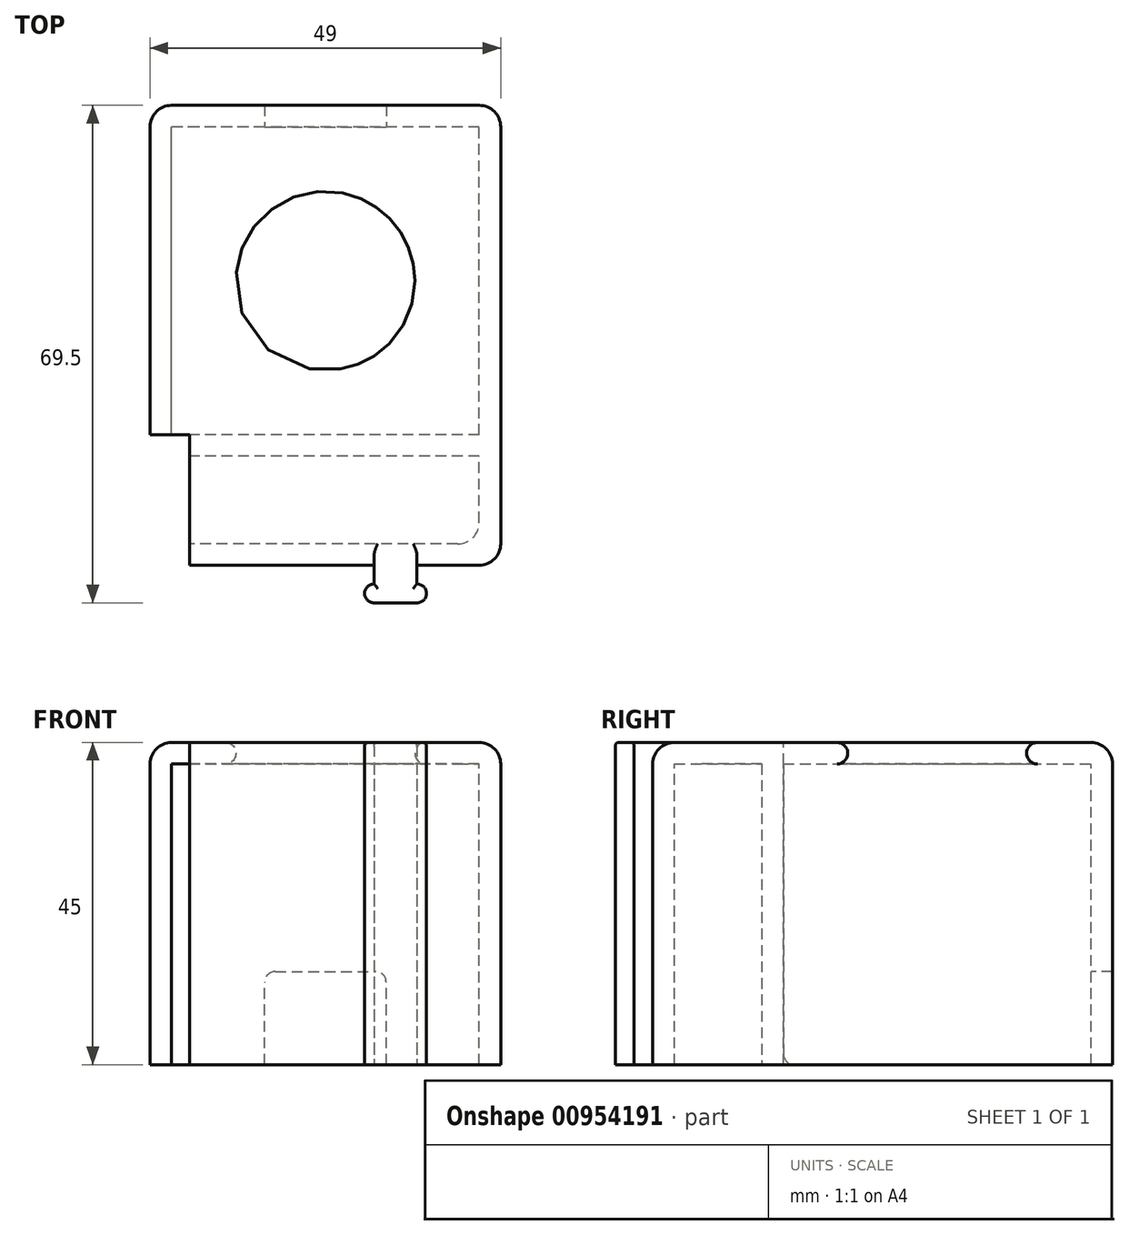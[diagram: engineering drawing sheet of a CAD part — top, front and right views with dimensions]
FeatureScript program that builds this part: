
annotation { "Feature Type Name" : "Feature", "Feature Type Description" : "" }
export const myFeature = defineFeature(function(context is Context, id is Id, definition is map)
    precondition{}
    {
        {
            var Q0;
            Q0=qCreatedBy(makeId("Top.planeOp"),FACE);
            var sketch = newSketch(context, id + "F0", { "sketchPlane" : qUnion([Q0])});
            skLineSegment(sketch, "E0.bottom", {"start": v(21.5, -21.5) * mm, "end": v(-21.5, -21.5) * mm});
            skLineSegment(sketch, "E0.top", {"start": v(21.5, 21.5) * mm, "end": v(-21.5, 21.5) * mm});
            skLineSegment(sketch, "E0.left", {"start": v(21.5, -21.5) * mm, "end": v(21.5, 21.5) * mm});
            skLineSegment(sketch, "E0.right", {"start": v(-21.5, -21.5) * mm, "end": v(-21.5, 21.5) * mm});
            skPoint(sketch, "E0.middle", {"position": v(0, 0) * mm});
            skLineSegment(sketch, "E1.0", {"start": v(24.5, -24.5) * mm, "end": v(24.5, 24.5) * mm});
            skLineSegment(sketch, "E1.1", {"start": v(24.5, -24.5) * mm, "end": v(-24.5, -24.5) * mm});
            skLineSegment(sketch, "E1.2", {"start": v(-24.5, -24.5) * mm, "end": v(-24.5, 24.5) * mm});
            skLineSegment(sketch, "E1.3", {"start": v(24.5, 24.5) * mm, "end": v(-24.5, 24.5) * mm});
            skSolve(sketch);
        }
        {
            var Q0;
            Q0=makeQuery(id+"F0.imprint","IMPRINT",FACE,{"disambiguationData":[TD([[makeQuery(id+"F0.imprint","IMPRINT",EDGE,{"derivedFrom":sQuery(id+"F0.wireOp",EDGE,"E0.bottom")}),1.0]])]});
            extrude(context, id + "F1", {"entities" : qUnion([Q0]), "oppositeDirection" : true, "depth" : 42 * mm, "offsetDistance" : 25 * mm});
        }
        {
            var Q0;
            Q0=makeQuery(id+"F0.imprint","IMPRINT",FACE,{"disambiguationData":[TD([[makeQuery(id+"F0.imprint","IMPRINT",EDGE,{"derivedFrom":sQuery(id+"F0.wireOp",EDGE,"E0.bottom")}),-1.0]])]});
            var Q1;
            Q1=makeQuery(id+"F0.imprint","IMPRINT",FACE,{"disambiguationData":[TD([[makeQuery(id+"F0.imprint","IMPRINT",EDGE,{"derivedFrom":sQuery(id+"F0.wireOp",EDGE,"E0.bottom")}),1.0]])]});
            extrude(context, id + "F2", {"entities" : qUnion([Q0, Q1]), "operationType" : NewBodyOperationType.ADD, "depth" : 3 * mm, "offsetDistance" : 25 * mm});
        }
        {
            var Q0;
            Q0=qCreatedBy(makeId("Top.planeOp"),FACE);
            var sketch = newSketch(context, id + "F3", { "sketchPlane" : qUnion([Q0])});
            skCircle(sketch, "E2", {"center": v(0, 0) * mm, "radius": 12.5 * mm});
            skSolve(sketch);
        }
        {
            var Q0;
            Q0=qSketchRegion(id+"F3",true);
            extrude(context, id + "F4", {"entities" : qUnion([Q0]), "operationType" : NewBodyOperationType.REMOVE, "endBound" : BoundingType.THROUGH_ALL, "depth" : 25 * mm, "offsetDistance" : 25 * mm});
        }
        {
            var Q0;
            Q0=qCreatedBy(makeId("Front.planeOp"),FACE);
            var sketch = newSketch(context, id + "F5", { "sketchPlane" : qUnion([Q0])});
            skLineSegment(sketch, "E3.bottom", {"start": v(8.5, -29) * mm, "end": v(-8.5, -29) * mm});
            skLineSegment(sketch, "E4", {"start": v(8.5, -42) * mm, "end": v(-8.5, -42) * mm});
            skLineSegment(sketch, "E5", {"start": v(0, 0) * mm, "end": v(0, -42) * mm, "construction": true});
            skLineSegment(sketch, "E6", {"start": v(8.5, -29) * mm, "end": v(8.5, -42) * mm});
            skLineSegment(sketch, "E7", {"start": v(-8.5, -29) * mm, "end": v(-8.5, -42) * mm});
            skSolve(sketch);
        }
        {
            var Q0;
            Q0=qSketchRegion(id+"F5",true);
            extrude(context, id + "F6", {"entities" : qUnion([Q0]), "operationType" : NewBodyOperationType.REMOVE, "endBound" : BoundingType.THROUGH_ALL, "oppositeDirection" : true, "depth" : 25 * mm, "offsetDistance" : 25 * mm});
        }
        {
            var Q0;
            Q0=qCreatedBy(makeId("Top.planeOp"),FACE);
            var sketch = newSketch(context, id + "F7", { "sketchPlane" : qUnion([Q0])});
            skLineSegment(sketch, "E8.bottom", {"start": v(-24.5, -24.5) * mm, "end": v(24.5, -24.5) * mm});
            skLineSegment(sketch, "E8.top", {"start": v(-24.5, -39.75) * mm, "end": v(24.5, -39.75) * mm});
            skLineSegment(sketch, "E8.left", {"start": v(-24.5, -24.5) * mm, "end": v(-24.5, -39.75) * mm});
            skLineSegment(sketch, "E8.right", {"start": v(24.5, -24.5) * mm, "end": v(24.5, -39.75) * mm});
            skLineSegment(sketch, "E9.0", {"start": v(-21.5, -24.5) * mm, "end": v(-21.5, -36.75) * mm});
            skLineSegment(sketch, "E9.2", {"start": v(21.5, -24.5) * mm, "end": v(21.5, -36.75) * mm});
            skLineSegment(sketch, "E9.3", {"start": v(-21.5, -36.75) * mm, "end": v(21.5, -36.75) * mm});
            skSolve(sketch);
        }
        {
            var Q0;
            Q0=makeQuery(id+"F7.imprint","IMPRINT",FACE,{"disambiguationData":[TD([[makeQuery(id+"F7.imprint","IMPRINT",EDGE,{"derivedFrom":sQuery(id+"F7.wireOp",EDGE,"E8.bottom")}),-1.0]])]});
            var Q1;
            Q1=makeQuery(id+"F1.opExtrude","CAP_FACE",FACE,{"disambiguationData":[OSD([sQuery(id+"F0.wireOp",EDGE,"E0.bottom"),sQuery(id+"F0.wireOp",EDGE,"E0.top"),sQuery(id+"F0.wireOp",EDGE,"E0.left"),sQuery(id+"F0.wireOp",EDGE,"E0.right"),sQuery(id+"F0.wireOp",EDGE,"E1.0"),sQuery(id+"F0.wireOp",EDGE,"E1.1"),sQuery(id+"F0.wireOp",EDGE,"E1.2"),sQuery(id+"F0.wireOp",EDGE,"E1.3")])],"isStart":false});
            var Q2;
            Q2=makeQuery(id+"F2.opExtrude","CAP_FACE",FACE,{"disambiguationData":[OSD([sQuery(id+"F0.wireOp",EDGE,"E1.0"),sQuery(id+"F0.wireOp",EDGE,"E1.1"),sQuery(id+"F0.wireOp",EDGE,"E1.2"),sQuery(id+"F0.wireOp",EDGE,"E1.3")])],"isStart":false});
            extrude(context, id + "F8", {"entities" : qUnion([Q0]), "operationType" : NewBodyOperationType.ADD, "endBound" : BoundingType.UP_TO_SURFACE, "oppositeDirection" : true, "depth" : 25 * mm, "endBoundEntityFace" : qUnion([Q1]), "offsetDistance" : 25 * mm});
        }
        {
            var Q0;
            Q0=makeQuery(id+"F7.imprint","IMPRINT",FACE,{"disambiguationData":[TD([[makeQuery(id+"F7.imprint","IMPRINT",EDGE,{"derivedFrom":sQuery(id+"F7.wireOp",EDGE,"E9.0")}),1.0]])]});
            var Q1;
            Q1=makeQuery(id+"F7.imprint","IMPRINT",FACE,{"disambiguationData":[TD([[makeQuery(id+"F7.imprint","IMPRINT",EDGE,{"derivedFrom":sQuery(id+"F7.wireOp",EDGE,"E8.bottom")}),-1.0]])]});
            var Q2;
            Q2=makeQuery(id+"F2.opExtrude","CAP_FACE",FACE,{"disambiguationData":[OSD([sQuery(id+"F0.wireOp",EDGE,"E1.0"),sQuery(id+"F0.wireOp",EDGE,"E1.1"),sQuery(id+"F0.wireOp",EDGE,"E1.2"),sQuery(id+"F0.wireOp",EDGE,"E1.3")])],"isStart":false});
            extrude(context, id + "F9", {"entities" : qUnion([Q0, Q1]), "operationType" : NewBodyOperationType.ADD, "endBound" : BoundingType.UP_TO_SURFACE, "depth" : 25 * mm, "endBoundEntityFace" : qUnion([Q2]), "offsetDistance" : 25 * mm});
        }
        {
            var Q0;
            Q0=qCreatedBy(makeId("Top.planeOp"),FACE);
            var sketch = newSketch(context, id + "F10", { "sketchPlane" : qUnion([Q0])});
            skLineSegment(sketch, "E10.bottom", {"start": v(6.8, -39.75) * mm, "end": v(12.8, -39.75) * mm});
            skLineSegment(sketch, "E10.top", {"start": v(6.8, -45) * mm, "end": v(12.8, -45) * mm});
            skLineSegment(sketch, "E10.left", {"start": v(6.8, -39.75) * mm, "end": v(6.8, -42.35) * mm});
            skLineSegment(sketch, "E10.right", {"start": v(12.8, -39.75) * mm, "end": v(12.8, -42.35) * mm});
            skArc(sketch, "E11", {"start": v(6.8, -42.35) * mm, "mid": v(5.47, -43.68) * mm, "end": v(6.8, -45) * mm});
            skArc(sketch, "E12", {"start": v(12.8, -45) * mm, "mid": v(14.12, -43.68) * mm, "end": v(12.8, -42.35) * mm});
            skSolve(sketch);
        }
        {
            var Q0;
            Q0=qSketchRegion(id+"F10",true);
            var Q1;
            Q1=makeQuery(id+"F2.opExtrude","CAP_FACE",FACE,{"disambiguationData":[OSD([sQuery(id+"F0.wireOp",EDGE,"E1.0"),sQuery(id+"F0.wireOp",EDGE,"E1.1"),sQuery(id+"F0.wireOp",EDGE,"E1.2"),sQuery(id+"F0.wireOp",EDGE,"E1.3")])],"isStart":false});
            var Q2;
            Q2=makeQuery(id+"F1.opExtrude","CAP_FACE",FACE,{"disambiguationData":[OSD([sQuery(id+"F0.wireOp",EDGE,"E0.bottom"),sQuery(id+"F0.wireOp",EDGE,"E0.top"),sQuery(id+"F0.wireOp",EDGE,"E0.left"),sQuery(id+"F0.wireOp",EDGE,"E0.right"),sQuery(id+"F0.wireOp",EDGE,"E1.0"),sQuery(id+"F0.wireOp",EDGE,"E1.1"),sQuery(id+"F0.wireOp",EDGE,"E1.2"),sQuery(id+"F0.wireOp",EDGE,"E1.3")])],"isStart":false});
            extrude(context, id + "F11", {"entities" : qUnion([Q0]), "operationType" : NewBodyOperationType.ADD, "endBound" : BoundingType.UP_TO_SURFACE, "depth" : 25 * mm, "endBoundEntityFace" : qUnion([Q1]), "offsetDistance" : 25 * mm, "hasSecondDirection" : true, "secondDirectionBound" : SecondDirectionBoundingType.UP_TO_SURFACE, "secondDirectionOppositeDirection" : true, "secondDirectionDepth" : 25 * mm, "secondDirectionBoundEntityFace" : qUnion([Q2])});
        }
        {
            var Q0;
            Q0=qCreatedBy(makeId("Right.planeOp"),FACE);
            cPlane(context, id + "F12", {"entities" : qUnion([Q0]), "cplaneType" : CPlaneType.OFFSET, "offset" : 19 * mm, "oppositeDirection" : true, "width" : 150 * mm, "height" : 150 * mm});
        }
        {
            var Q0;
            Q0=qCreatedBy(id+"F12.planeOp",FACE);
            var sketch = newSketch(context, id + "F13", { "sketchPlane" : qUnion([Q0])});
            skLineSegment(sketch, "E13.bottom", {"start": v(-21.5, -42) * mm, "end": v(-39.75, -42) * mm});
            skLineSegment(sketch, "E13.top", {"start": v(-21.5, 3) * mm, "end": v(-39.75, 3) * mm});
            skLineSegment(sketch, "E13.left", {"start": v(-21.5, -42) * mm, "end": v(-21.5, 3) * mm});
            skLineSegment(sketch, "E13.right", {"start": v(-39.75, -42) * mm, "end": v(-39.75, 3) * mm});
            skSolve(sketch);
        }
        {
            var Q0;
            Q0=qSketchRegion(id+"F13",true);
            var Q1;
            {var subQ0=sQuery(id+"F7.wireOp",EDGE,"E8.left");var subQ1=sQuery(id+"F0.wireOp",EDGE,"E1.2");Q1=makeQuery(id+"F9.boolean.opBoolean","MERGE",FACE,{"derivedFrom":[makeQuery(id+"F8.boolean.opBoolean","MERGE",FACE,{"derivedFrom":[makeQuery(id+"F2.boolean.opBoolean","MERGE",FACE,{"derivedFrom":[makeQuery(id+"F1.opExtrude","SWEPT_FACE",FACE,{"disambiguationData":[OSD([subQ1])]}),makeQuery(id+"F2.opExtrude","SWEPT_FACE",FACE,{"disambiguationData":[OSD([subQ1])]})]}),makeQuery(id+"F8.opExtrude","SWEPT_FACE",FACE,{"disambiguationData":[OSD([subQ0])]})]}),makeQuery(id+"F9.opExtrude","SWEPT_FACE",FACE,{"disambiguationData":[OSD([subQ0])]})]});}
            extrude(context, id + "F14", {"entities" : qUnion([Q0]), "operationType" : NewBodyOperationType.REMOVE, "endBound" : BoundingType.UP_TO_SURFACE, "oppositeDirection" : true, "depth" : 25 * mm, "endBoundEntityFace" : qUnion([Q1]), "offsetDistance" : 10 * mm, "offsetOppositeDirection" : true});
        }
        {
            var Q0;
            Q0=makeQuery(id+"F1.opExtrude","SWEPT_EDGE",EDGE,{"disambiguationData":[OSD([sQuery(id+"F0.wireOp",EDGE,"E1.1"),sQuery(id+"F0.wireOp",EDGE,"E1.2")])]});
            var Q1;
            Q1=makeQuery(id+"F1.opExtrude","SWEPT_EDGE",EDGE,{"disambiguationData":[OSD([sQuery(id+"F0.wireOp",EDGE,"E1.0"),sQuery(id+"F0.wireOp",EDGE,"E1.1")])]});
            var Q2;
            Q2=makeQuery(id+"F1.opExtrude","SWEPT_EDGE",EDGE,{"disambiguationData":[OSD([sQuery(id+"F0.wireOp",EDGE,"E1.0"),sQuery(id+"F0.wireOp",EDGE,"E1.3")])]});
            var Q3;
            Q3=makeQuery(id+"F1.opExtrude","SWEPT_EDGE",EDGE,{"disambiguationData":[OSD([sQuery(id+"F0.wireOp",EDGE,"E1.2"),sQuery(id+"F0.wireOp",EDGE,"E1.3")])]});
            var Q4;
            Q4=makeQuery(id+"F2.opExtrude","CAP_EDGE",EDGE,{"disambiguationData":[OSD([sQuery(id+"F0.wireOp",EDGE,"E1.2")])],"isStart":false});
            var Q5;
            Q5=makeQuery(id+"F2.opExtrude","CAP_EDGE",EDGE,{"disambiguationData":[OSD([sQuery(id+"F0.wireOp",EDGE,"E1.1")])],"isStart":false});
            var Q6;
            Q6=makeQuery(id+"F2.opExtrude","CAP_EDGE",EDGE,{"disambiguationData":[OSD([sQuery(id+"F0.wireOp",EDGE,"E1.0")])],"isStart":false});
            var Q7;
            Q7=makeQuery(id+"F2.opExtrude","CAP_EDGE",EDGE,{"disambiguationData":[OSD([sQuery(id+"F0.wireOp",EDGE,"E1.3")])],"isStart":false});
            var Q8;
            Q8=makeQuery(id+"F8.opExtrude","TWEAK_EDGE",EDGE,{"derivedFrom":[makeQuery(id+"F7.imprint","IMPRINT",EDGE,{"derivedFrom":sQuery(id+"F7.wireOp",EDGE,"E8.top")}),makeQuery(id+"F7.imprint","IMPRINT",EDGE,{"derivedFrom":sQuery(id+"F7.wireOp",EDGE,"E8.right")})]});
            var Q9;
            Q9=makeQuery(id+"F8.opExtrude","TWEAK_EDGE",EDGE,{"derivedFrom":[makeQuery(id+"F7.imprint","IMPRINT",EDGE,{"derivedFrom":sQuery(id+"F7.wireOp",EDGE,"E8.top")}),makeQuery(id+"F7.imprint","IMPRINT",EDGE,{"derivedFrom":sQuery(id+"F7.wireOp",EDGE,"E8.left")})]});
            var Q10;
            {var subQ1=sQuery(id+"F7.wireOp",EDGE,"E8.top");var subQ2=sQuery(id+"F0.wireOp",EDGE,"E1.2");Q10=makeQuery(id+"F11.boolean.opBoolean","SPLIT",EDGE,{"disambiguationData":[TD([makeQuery(id+"F1.opExtrude","SWEPT_FACE",FACE,{"disambiguationData":[OSD([subQ2])]})])],"derivedFrom":makeQuery(id+"F8.opExtrude","CAP_EDGE",EDGE,{"disambiguationData":[OSD([subQ1])],"isStart":true})});}
            var Q11;
            {var subQ1=sQuery(id+"F7.wireOp",EDGE,"E8.top");var subQ2=sQuery(id+"F0.wireOp",EDGE,"E1.0");Q11=makeQuery(id+"F11.boolean.opBoolean","SPLIT",EDGE,{"disambiguationData":[TD([makeQuery(id+"F1.opExtrude","SWEPT_FACE",FACE,{"disambiguationData":[OSD([subQ2])]})])],"derivedFrom":makeQuery(id+"F8.opExtrude","CAP_EDGE",EDGE,{"disambiguationData":[OSD([subQ1])],"isStart":true})});}
            var Q12;
            {var subQ0=sQuery(id+"F7.wireOp",EDGE,"E8.top");var subQ1=sQuery(id+"F10.wireOp",EDGE,"E10.left");Q12=makeQuery(id+"F11.boolean.opBoolean","SPLIT",EDGE,{"disambiguationData":[TD([makeQuery(id+"F11.opExtrude","SWEPT_FACE",FACE,{"disambiguationData":[OSD([subQ1])]})])],"derivedFrom":makeQuery(id+"F8.opExtrude","CAP_EDGE",EDGE,{"disambiguationData":[OSD([subQ0])],"isStart":true})});}
            var Q13;
            {var subQ0=sQuery(id+"F7.wireOp",EDGE,"E8.right");var subQ1=sQuery(id+"F7.wireOp",EDGE,"E8.top");Q13=makeQuery(id+"F9.boolean.opBoolean","MERGE",EDGE,{"derivedFrom":[makeQuery(id+"F8.opExtrude","SWEPT_EDGE",EDGE,{"disambiguationData":[OSD([subQ1,subQ0])]}),makeQuery(id+"F9.opExtrude","SWEPT_EDGE",EDGE,{"disambiguationData":[OSD([subQ1,subQ0])]})]});}
            var Q14;
            {var subQ2=sQuery(id+"F7.wireOp",EDGE,"E8.top");var subQ3=sQuery(id+"F0.wireOp",EDGE,"E1.0");Q14=makeQuery(id+"F11.boolean.opBoolean","SPLIT",EDGE,{"disambiguationData":[TD([makeQuery(id+"F1.opExtrude","SWEPT_FACE",FACE,{"disambiguationData":[OSD([subQ3])]})])],"derivedFrom":makeQuery(id+"F9.opExtrude","CAP_EDGE",EDGE,{"disambiguationData":[OSD([subQ2])],"isStart":false})});}
            var Q15;
            {var subQ0=sQuery(id+"F7.wireOp",EDGE,"E8.top");var subQ2=sQuery(id+"F10.wireOp",EDGE,"E10.left");Q15=makeQuery(id+"F11.boolean.opBoolean","SPLIT",EDGE,{"disambiguationData":[TD([makeQuery(id+"F11.opExtrude","SWEPT_FACE",FACE,{"disambiguationData":[OSD([subQ2])]})])],"derivedFrom":makeQuery(id+"F9.opExtrude","CAP_EDGE",EDGE,{"disambiguationData":[OSD([subQ0])],"isStart":false})});}
            var Q16;
            {var subQ2=sQuery(id+"F7.wireOp",EDGE,"E8.top");var subQ3=sQuery(id+"F0.wireOp",EDGE,"E1.2");Q16=makeQuery(id+"F11.boolean.opBoolean","SPLIT",EDGE,{"disambiguationData":[TD([makeQuery(id+"F1.opExtrude","SWEPT_FACE",FACE,{"disambiguationData":[OSD([subQ3])]})])],"derivedFrom":makeQuery(id+"F9.opExtrude","CAP_EDGE",EDGE,{"disambiguationData":[OSD([subQ2])],"isStart":false})});}
            var Q17;
            {var subQ0=sQuery(id+"F7.wireOp",EDGE,"E8.left");var subQ1=sQuery(id+"F7.wireOp",EDGE,"E8.top");Q17=makeQuery(id+"F9.boolean.opBoolean","MERGE",EDGE,{"derivedFrom":[makeQuery(id+"F8.opExtrude","SWEPT_EDGE",EDGE,{"disambiguationData":[OSD([subQ1,subQ0])]}),makeQuery(id+"F9.opExtrude","SWEPT_EDGE",EDGE,{"disambiguationData":[OSD([subQ1,subQ0])]})]});}
            var Q18;
            Q18=makeQuery(id+"F8.opExtrude","SWEPT_EDGE",EDGE,{"disambiguationData":[OSD([sQuery(id+"F7.wireOp",EDGE,"E8.bottom"),sQuery(id+"F7.wireOp",EDGE,"E9.2")])]});
            var Q19;
            Q19=makeQuery(id+"F9.opExtrude","CAP_EDGE",EDGE,{"disambiguationData":[OSD([sQuery(id+"F7.wireOp",EDGE,"E8.bottom")])],"isStart":true});
            var Q20;
            Q20=makeQuery(id+"F8.opExtrude","CAP_EDGE",EDGE,{"disambiguationData":[OSD([sQuery(id+"F7.wireOp",EDGE,"E9.3")])],"isStart":true});
            var Q21;
            Q21=makeQuery(id+"F8.opExtrude","SWEPT_EDGE",EDGE,{"disambiguationData":[OSD([sQuery(id+"F7.wireOp",EDGE,"E9.2"),sQuery(id+"F7.wireOp",EDGE,"E9.3")])]});
            fillet(context, id + "F15", {"entities" : qUnion([Q0, Q1, Q2, Q3, Q4, Q5, Q6, Q7, Q8, Q9, Q10, Q11, Q12, Q13, Q14, Q15, Q16, Q17, Q18, Q19, Q20, Q21]), "radius" : 3 * mm, "tangentPropagation" : true, "allowEdgeOverflow" : false});
        }
        {
            var Q0;
            Q0=makeQuery(id+"F4.boolean.opBoolean","COPY",FACE,{"derivedFrom":makeQuery(id+"F4.opExtrude","SWEPT_FACE",FACE,{"disambiguationData":[OSD([sQuery(id+"F3.wireOp",EDGE,"E2")])]})});
            fillet(context, id + "F16", {"entities" : qUnion([Q0]), "radius" : 1.5 * mm, "tangentPropagation" : true, "allowEdgeOverflow" : false});
        }
        {
            var Q0;
            Q0=makeQuery(id+"F6.boolean.opBoolean","COPY",EDGE,{"derivedFrom":makeQuery(id+"F6.opExtrude","SWEPT_EDGE",EDGE,{"disambiguationData":[OSD([sQuery(id+"F5.wireOp",EDGE,"E3.bottom"),sQuery(id+"F5.wireOp",EDGE,"NUcqTPHW-UgJx-RYx9-z1JQ-IcGqAazsJhif")])]})});
            var Q1;
            Q1=makeQuery(id+"F6.boolean.opBoolean","COPY",EDGE,{"derivedFrom":makeQuery(id+"F6.opExtrude","SWEPT_EDGE",EDGE,{"disambiguationData":[OSD([sQuery(id+"F5.wireOp",EDGE,"NUcqTPHW-UgJx-RYx9-z1JQ-IcGqAazsJhif"),sQuery(id+"F5.wireOp",EDGE,"E4")])]})});
            var Q2;
            Q2=makeQuery(id+"F6.boolean.opBoolean","COPY",EDGE,{"derivedFrom":makeQuery(id+"F6.opExtrude","SWEPT_EDGE",EDGE,{"disambiguationData":[OSD([sQuery(id+"F5.wireOp",EDGE,"E3.bottom"),sQuery(id+"F5.wireOp",EDGE,"tBwVpeCi-kpxs-Gkok-rJm8-Y1xPES7qzH3W")])]})});
            var Q3;
            Q3=makeQuery(id+"F6.boolean.opBoolean","COPY",EDGE,{"derivedFrom":makeQuery(id+"F6.opExtrude","SWEPT_EDGE",EDGE,{"disambiguationData":[OSD([sQuery(id+"F5.wireOp",EDGE,"tBwVpeCi-kpxs-Gkok-rJm8-Y1xPES7qzH3W"),sQuery(id+"F5.wireOp",EDGE,"E4")])]})});
            var Q4;
            {var subQ0=sQuery(id+"F7.wireOp",EDGE,"E8.top");var subQ2=sQuery(id+"F13.wireOp",EDGE,"E13.bottom");Q4=makeQuery(id+"F14.boolean.opBoolean","COPY",EDGE,{"disambiguationData":[TD([makeQuery(id+"F8.opExtrude","SWEPT_FACE",FACE,{"disambiguationData":[OSD([subQ0])]})])],"derivedFrom":makeQuery(id+"F14.opExtrude","CAP_EDGE",EDGE,{"disambiguationData":[OSD([subQ2])],"isStart":true})});}
            var Q5;
            {var subQ0=sQuery(id+"F13.wireOp",EDGE,"E13.top");var subQ1=sQuery(id+"F7.wireOp",EDGE,"E8.top");Q5=makeQuery(id+"F14.boolean.opBoolean","COPY",EDGE,{"disambiguationData":[TD([makeQuery(id+"F8.opExtrude","SWEPT_FACE",FACE,{"disambiguationData":[OSD([subQ1])]})])],"derivedFrom":makeQuery(id+"F14.opExtrude","CAP_EDGE",EDGE,{"disambiguationData":[OSD([subQ0])],"isStart":true})});}
            var Q6;
            {var subQ0=sQuery(id+"F13.wireOp",EDGE,"E13.top");var subQ1=sQuery(id+"F13.wireOp",EDGE,"E13.left");Q6=makeQuery(id+"F14.boolean.opBoolean","COPY",EDGE,{"disambiguationData":[topologyDisambiguationEdgeConnected([makeQuery(id+"F14.opExtrude","SWEPT_FACE",FACE,{"disambiguationData":[OSD([subQ1])]})])],"derivedFrom":makeQuery(id+"F14.opExtrude","SWEPT_EDGE",EDGE,{"disambiguationData":[OSD([subQ0,subQ1])]})});}
            var Q7;
            Q7=makeQuery(id+"F14.boolean.opBoolean","COPY",EDGE,{"derivedFrom":makeQuery(id+"F14.opExtrude","SWEPT_EDGE",EDGE,{"disambiguationData":[OSD([sQuery(id+"F13.wireOp",EDGE,"E13.bottom"),sQuery(id+"F13.wireOp",EDGE,"E13.left")])]})});
            var Q8;
            {var subQ0=sQuery(id+"F13.wireOp",EDGE,"E13.top");Q8=makeQuery(id+"F14.boolean.opBoolean","COPY",EDGE,{"disambiguationData":[TD([makeQuery(id+"F1.opExtrude","SWEPT_FACE",FACE,{"disambiguationData":[OSD([sQuery(id+"F0.wireOp",EDGE,"E0.bottom")])]})])],"derivedFrom":makeQuery(id+"F14.opExtrude","CAP_EDGE",EDGE,{"disambiguationData":[OSD([subQ0])],"isStart":true})});}
            var Q9;
            {var subQ0=sQuery(id+"F0.wireOp",EDGE,"E0.bottom");var subQ2=sQuery(id+"F13.wireOp",EDGE,"E13.bottom");Q9=makeQuery(id+"F14.boolean.opBoolean","COPY",EDGE,{"disambiguationData":[TD([makeQuery(id+"F1.opExtrude","SWEPT_FACE",FACE,{"disambiguationData":[OSD([subQ0])]})])],"derivedFrom":makeQuery(id+"F14.opExtrude","CAP_EDGE",EDGE,{"disambiguationData":[OSD([subQ2])],"isStart":true})});}
            fillet(context, id + "F17", {"entities" : qUnion([Q0, Q1, Q2, Q3, Q4, Q5, Q6, Q7, Q8, Q9]), "radius" : 1.5 * mm, "tangentPropagation" : true, "allowEdgeOverflow" : false});
        }
        {
            var Q0;
            Q0=makeQuery(id+"FnS4vniIDeti8Xd_1.1.F11.opExtrude","CAP_EDGE",EDGE,{"disambiguationData":[OSD([sQuery(id+"F10.wireOp",EDGE,"E10.left")])],"isStart":false});
            var Q1;
            Q1=makeQuery(id+"FnS4vniIDeti8Xd_1.1.F11.opExtrude","CAP_EDGE",EDGE,{"disambiguationData":[OSD([sQuery(id+"F10.wireOp",EDGE,"E10.right")])],"isStart":false});
            var Q2;
            Q2=makeQuery(id+"FnS4vniIDeti8Xd_1.1.F11.opExtrude","CAP_EDGE",EDGE,{"disambiguationData":[OSD([sQuery(id+"F10.wireOp",EDGE,"E12")])],"isStart":false});
            var Q3;
            Q3=makeQuery(id+"FnS4vniIDeti8Xd_1.1.F11.opExtrude","CAP_EDGE",EDGE,{"disambiguationData":[OSD([sQuery(id+"F10.wireOp",EDGE,"E11")])],"isStart":false});
            var Q4;
            Q4=makeQuery(id+"FnS4vniIDeti8Xd_1.1.F11.opExtrude","CAP_EDGE",EDGE,{"disambiguationData":[OSD([sQuery(id+"F10.wireOp",EDGE,"E10.top")])],"isStart":false});
            var Q5;
            Q5=makeQuery(id+"F11.opExtrude","CAP_EDGE",EDGE,{"disambiguationData":[OSD([sQuery(id+"F10.wireOp",EDGE,"E11")])],"isStart":false});
            var Q6;
            Q6=makeQuery(id+"F11.opExtrude","CAP_EDGE",EDGE,{"disambiguationData":[OSD([sQuery(id+"F10.wireOp",EDGE,"E10.left")])],"isStart":false});
            var Q7;
            Q7=makeQuery(id+"F11.opExtrude","CAP_EDGE",EDGE,{"disambiguationData":[OSD([sQuery(id+"F10.wireOp",EDGE,"E10.right")])],"isStart":false});
            var Q8;
            Q8=makeQuery(id+"F11.opExtrude","CAP_EDGE",EDGE,{"disambiguationData":[OSD([sQuery(id+"F10.wireOp",EDGE,"E12")])],"isStart":false});
            var Q9;
            Q9=makeQuery(id+"F11.opExtrude","CAP_EDGE",EDGE,{"disambiguationData":[OSD([sQuery(id+"F10.wireOp",EDGE,"E10.top")])],"isStart":false});
            fillet(context, id + "F18", {"entities" : qUnion([Q0, Q1, Q2, Q3, Q4, Q5, Q6, Q7, Q8, Q9]), "radius" : .5 * mm, "tangentPropagation" : true, "allowEdgeOverflow" : false});
        }
    });
